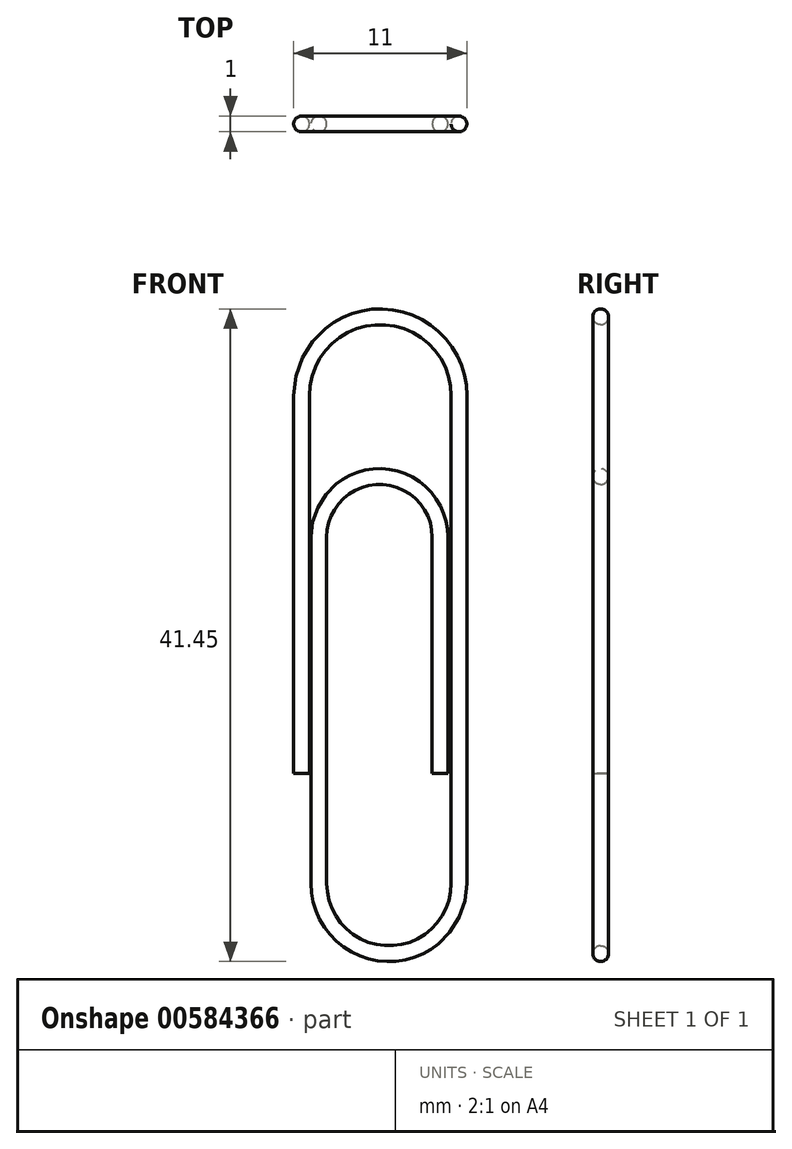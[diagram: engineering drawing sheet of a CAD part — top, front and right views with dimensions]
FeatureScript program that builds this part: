
annotation { "Feature Type Name" : "Feature", "Feature Type Description" : "" }
export const myFeature = defineFeature(function(context is Context, id is Id, definition is map)
    precondition{}
    {
        {
            var Q0;
            Q0=qCreatedBy(makeId("Front.planeOp"),FACE);
            var sketch = newSketch(context, id + "F0", { "sketchPlane" : qUnion([Q0])});
            skLineSegment(sketch, "E0", {"start": v(0, 0) * mm, "end": v(0, 24) * mm});
            skLineSegment(sketch, "E1", {"start": v(10, 24) * mm, "end": v(10, -7) * mm});
            skLineSegment(sketch, "E2", {"start": v(1.1, -7) * mm, "end": v(1.1, 15) * mm});
            skLineSegment(sketch, "E3", {"start": v(8.8, 15) * mm, "end": v(8.8, 0) * mm});
            skArc(sketch, "E4", {"start": v(10, 24) * mm, "mid": v(5, 29) * mm, "end": v(0, 24) * mm});
            skArc(sketch, "E5", {"start": v(1.1, -7) * mm, "mid": v(5.55, -11.45) * mm, "end": v(10, -7) * mm});
            skArc(sketch, "E6", {"start": v(8.8, 15) * mm, "mid": v(4.95, 18.85) * mm, "end": v(1.1, 15) * mm});
            skSolve(sketch);
        }
        {
            var Q0;
            Q0=qCreatedBy(makeId("Top.planeOp"),FACE);
            var sketch = newSketch(context, id + "F1", { "sketchPlane" : qUnion([Q0])});
            skCircle(sketch, "E7", {"center": v(0, 0) * mm, "radius": 0.5 * mm});
            skSolve(sketch);
        }
        {
            var Q0;
            Q0=makeQuery(id+"F1.imprint","IMPRINT",FACE,{"disambiguationData":[TD([[makeQuery(id+"F1.imprint","IMPRINT",EDGE,{"derivedFrom":sQuery(id+"F1.wireOp",EDGE,"E7")}),1.0]])]});
            var Q1;
            Q1=sQuery(id+"F0.wireOp",EDGE,"E0");
            var Q2;
            Q2=sQuery(id+"F0.wireOp",EDGE,"E4");
            var Q3;
            Q3=sQuery(id+"F0.wireOp",EDGE,"E1");
            var Q4;
            Q4=sQuery(id+"F0.wireOp",EDGE,"E6");
            var Q5;
            Q5=sQuery(id+"F0.wireOp",EDGE,"E3");
            var Q6;
            Q6=sQuery(id+"F0.wireOp",EDGE,"E2");
            var Q7;
            Q7=sQuery(id+"F0.wireOp",EDGE,"E5");
            sweep(context, id + "F2", {"profiles" : qUnion([Q0]), "path" : qUnion([Q1, Q2, Q3, Q4, Q5, Q6, Q7])});
        }
    });
